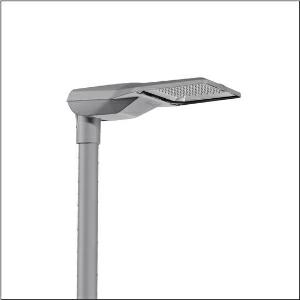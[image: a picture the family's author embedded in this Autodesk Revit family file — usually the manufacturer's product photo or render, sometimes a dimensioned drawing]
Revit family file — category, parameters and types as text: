
# Revit family: streetlight_sl_21_iq_midi___stw1_0a_5xe3e31g08nb_66c1
name_source: partatom
category: Lighting Fixtures
units: mm (PartAtom-declared; Revit-internal decimal feet)

## family parameters
Cut with Voids When Loaded = No
Host = Face
Light Source = No
Part Type = Normal
Room Calculation Point = No
Round Connector Dimension = Use Diameter
Shared = No

## types (1)
- --- (1 x LED, 23230 lm, 155.5 W, 3000K)
    Apparent Load = 155 VA
    CIE Flux Codes = 39 75 98 100 100
    Color Rendering = 70
    Color Temperature = 3000K
    Default Elevation = 1800 mm
    Description = Streetlight SL 21 iQ midi, mast luminaire, primary light control with lens, of PMMA, primary optical cover: cover, of toughened safety glass, transparent, light distribution: STW1.0a, light emission: direct distribution, primary light characteristic: asymmetric, installation type: post-top, side-entry, LED, High Power LED, rated luminous flux: 23.230lm, luminous efficacy: 149lm/W, light colour: 730, colour temperature: 3000K, control: Street-Remote, Auto-Match, Temp-Guard, Lumen-Switch, Night-Set, Smart-Wire, Light-Fading, Desk-Remote (wireless, voltage-free reading and setting of iQ features in the workshop via application-optimized NFC function/RFID function), optimised constant luminous flux control (CLO 2.0), presetting dimming linear, mains connection: 230..240V, AC, 50/60Hz, start of lifetime: 156W, end of service life: 162W, reduction: 69W, luminaire housing, of diecast aluminium, powder-coated, Siteco® metallic grey (DB 702S), corrosivity category C5 mid according to DIN EN ISO 12944, please order mast flange separately, inclination adjustable: 0°, 5°, 10°, 15°, sealing non-destructively replaceable, multi-level sealing system, length: 644mm, width: 335mm, height: 110mm, mast flange for spigot size: 42mm (side-entry): 5XC10008XM4, 60/48mm (side-entry/post-top): 5XC10108XM2, 76/60mm (side-entry/post-top): 5XC10108XM1, protection rating (complete): IP66, insulation class (complete): insulation class II (safety insulation), certification: CE, ENEC, ENEC+, VDE, impact resistance: IK09, permissible operating ambient temperature for outdoor applications: -40..+50°C, standard-compliant lighting for roads and squares, packaging unit: 1 piece

Light Distribution: STW1.0a
    Height = 111 mm
    Lamp = 1 x LED
    Lamp Light Flux = 23230 lm
    Lamp Power = 155.5 W
    Lamp count = 1
    Length = 644 mm
    Luminous efficacy = 149 lm/W
    Manufacturer = Siteco
    ModVariant = No
    Model = 5XE3E31G08NB
    Number of Poles = 1
    OnlyDefault = Yes
    Power Factor = 1
    Product Name = Streetlight SL 21 iQ midi | STW1.0a
    Product group = mast luminaire | pylon top
    ProductGroupID = 6100
    Protection Class = Protection class II
    Protection Degree = IP 66
    RLX_Detail_Level = 1
    RLX_Emergency_Light_Flux = 0 lm
    RLX_Emergency_Type = 0
    RLX_Emergency_Type_DB = No
    RlxData = <blob elided: 91265 chars, md5=79c37d5f>
    Socket = socket
    Standby Power = 0 W
    System Light Flux = 23230 lm
    System Power = 155 W
    Type Comments = factory setting: luminous flux: 100 % | dim-lin: 254 | 823 mA
    Type Image = l_1004298.jpg
    URL = http://relux.com
    VarID = @adj_102465
    Voltage = 0 V
    Weight = 0.00 kg
    Width = 336 mm

## geometry (parser evidence)
native form markers: Blend x4, Sweep x9
no freeform markers — native parametric forms only
